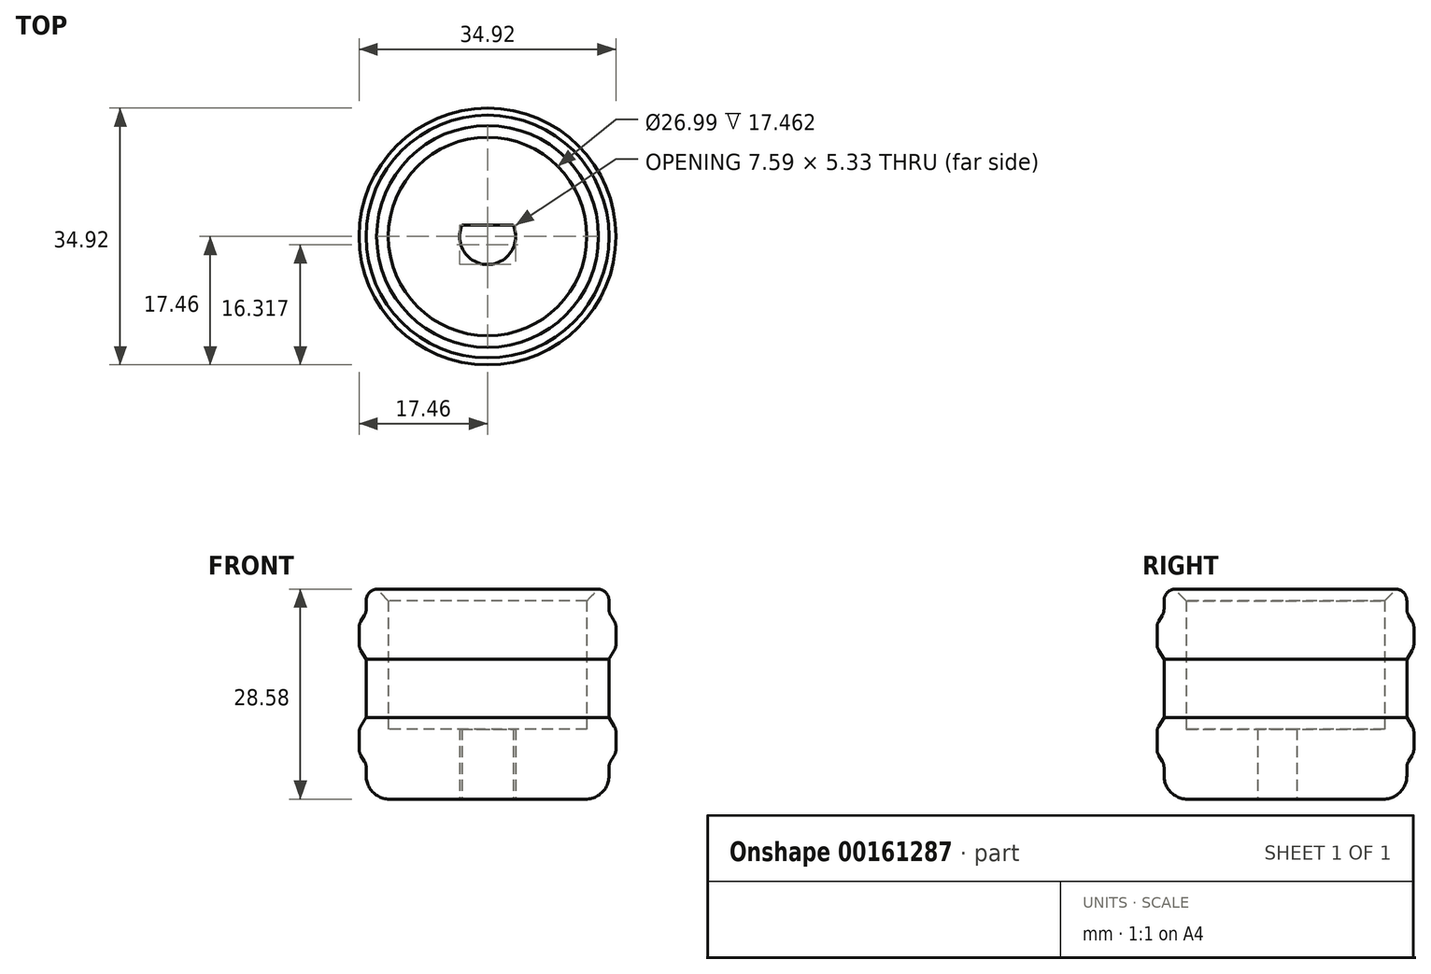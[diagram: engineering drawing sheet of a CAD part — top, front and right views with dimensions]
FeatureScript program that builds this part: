
annotation { "Feature Type Name" : "Feature", "Feature Type Description" : "" }
export const myFeature = defineFeature(function(context is Context, id is Id, definition is map)
    precondition{}
    {
        {
            var Q0;
            Q0=qCreatedBy(makeId("Top.planeOp"),FACE);
            var sketch = newSketch(context, id + "F0", { "sketchPlane" : qUnion([Q0])});
            skCircle(sketch, "E0", {"center": v(0, 0) * mm, "radius": 16.51 * mm});
            skArc(sketch, "E1", {"start": v(-3.5, 1.52) * mm, "mid": v(0, -3.81) * mm, "end": v(3.5, 1.52) * mm});
            skPoint(sketch, "E2", {"position": v(0, -3.81) * mm});
            skLineSegment(sketch, "E3", {"start": v(-3.5, 1.52) * mm, "end": v(3.5, 1.52) * mm});
            skSolve(sketch);
        }
        {
            var Q0;
            Q0=makeQuery(id+"F0.imprint","IMPRINT",FACE,{"disambiguationData":[TD([[makeQuery(id+"F0.imprint","IMPRINT",EDGE,{"derivedFrom":sQuery(id+"F0.wireOp",EDGE,"E0")}),1.0]])]});
            extrude(context, id + "F1", {"entities" : qUnion([Q0]), "depth" : 9.52 * mm, "offsetDistance" : 25.4 * mm});
        }
        {
            var Q0;
            Q0=makeQuery(id+"F1.opExtrude","CAP_FACE",FACE,{"disambiguationData":[OSD([sQuery(id+"F0.wireOp",EDGE,"E0"),sQuery(id+"F0.wireOp",EDGE,"E1"),sQuery(id+"F0.wireOp",EDGE,"E3")])],"isStart":false});
            var sketch = newSketch(context, id + "F2", { "sketchPlane" : qUnion([Q0])});
            skCircle(sketch, "E4", {"center": v(0, 0) * mm, "radius": 16.51 * mm});
            skCircle(sketch, "E5", {"center": v(0, 0) * mm, "radius": 13.5 * mm});
            skSolve(sketch);
        }
        {
            var Q0;
            Q0 = qSketchRegion(id + "F2", true);
            extrude(context, id + "F3", {"entities" : qUnion([Q0]), "operationType" : NewBodyOperationType.ADD, "depth" : 19.05 * mm, "offsetDistance" : 25.4 * mm});
        }
        {
            var Q0;
            Q0=makeQuery(id+"F3.opExtrude","CAP_EDGE",EDGE,{"disambiguationData":[OSD([sQuery(id+"F2.wireOp",EDGE,"E5")])],"isStart":false});
            chamfer(context, id + "F4", {"entities" : qUnion([Q0]), "width" : 1.59 * mm, "tangentPropagation" : true});
        }
        {
            var Q0;
            Q0=makeQuery(id+"F3.opExtrude","CAP_EDGE",EDGE,{"disambiguationData":[OSD([sQuery(id+"F2.wireOp",EDGE,"E4")])],"isStart":false});
            fillet(context, id + "F5", {"entities" : qUnion([Q0]), "radius" : 1.59 * mm, "tangentPropagation" : true, "allowEdgeOverflow" : false});
        }
        {
            var Q0;
            Q0=makeQuery(id+"F1.opExtrude","CAP_EDGE",EDGE,{"disambiguationData":[OSD([sQuery(id+"F0.wireOp",EDGE,"E0")])],"isStart":true});
            fillet(context, id + "F6", {"entities" : qUnion([Q0]), "radius" : 3.17 * mm, "tangentPropagation" : true, "allowEdgeOverflow" : false});
        }
        {
            var Q0;
            Q0=qCreatedBy(makeId("Right.planeOp"),FACE);
            var sketch = newSketch(context, id + "F7", { "sketchPlane" : qUnion([Q0])});
            skLineSegment(sketch, "E6", {"start": v(16.51, 25.4) * mm, "end": v(17.46, 23.81) * mm});
            skLineSegment(sketch, "E7", {"start": v(17.46, 23.81) * mm, "end": v(17.46, 20.64) * mm});
            skLineSegment(sketch, "E8", {"start": v(17.46, 20.64) * mm, "end": v(16.51, 19.05) * mm});
            skLineSegment(sketch, "E9", {"start": v(16.51, 19.05) * mm, "end": v(16.51, 25.4) * mm});
            skLineSegment(sketch, "E10", {"start": v(16.51, 11.11) * mm, "end": v(16.51, 4.76) * mm});
            skLineSegment(sketch, "E11", {"start": v(16.51, 4.76) * mm, "end": v(17.46, 6.35) * mm});
            skLineSegment(sketch, "E12", {"start": v(17.46, 6.35) * mm, "end": v(17.46, 9.53) * mm});
            skLineSegment(sketch, "E13", {"start": v(16.51, 11.11) * mm, "end": v(17.46, 9.53) * mm});
            skLineSegment(sketch, "E14", {"start": v(0, 41.62) * mm, "end": v(0, -11.38) * mm, "construction": true});
            skPoint(sketch, "E15", {"position": v(16.51, 22.22) * mm});
            skPoint(sketch, "E16", {"position": v(17.46, 22.22) * mm});
            skPoint(sketch, "E17", {"position": v(17.46, 7.94) * mm});
            skPoint(sketch, "E18", {"position": v(16.51, 7.94) * mm});
            skSolve(sketch);
        }
        {
            var Q0;
            Q0=makeQuery(id+"F7.imprint","IMPRINT",FACE,{"disambiguationData":[TD([[makeQuery(id+"F7.imprint","IMPRINT",EDGE,{"derivedFrom":sQuery(id+"F7.wireOp",EDGE,"E6")}),-1.0]])]});
            var Q1;
            Q1=makeQuery(id+"F7.imprint","IMPRINT",FACE,{"disambiguationData":[TD([[makeQuery(id+"F7.imprint","IMPRINT",EDGE,{"derivedFrom":sQuery(id+"F7.wireOp",EDGE,"E10")}),1.0]])]});
            var Q2;
            Q2=sQuery(id+"F7.wireOp",EDGE,"E14");
            revolve(context, id + "F8", {"operationType" : NewBodyOperationType.ADD, "surfaceOperationType" : NewSurfaceOperationType.NEW, "entities" : qUnion([Q0, Q1]), "axis" : qUnion([Q2]), "revolveType" : RevolveType.FULL});
        }
        {
            var Q0;
            Q0=makeQuery(id+"F8.opRevolve","SWEPT_EDGE",EDGE,{"disambiguationData":[OSD([sQuery(id+"F7.wireOp",EDGE,"E6"),sQuery(id+"F7.wireOp",EDGE,"E7")])]});
            var Q1;
            Q1=makeQuery(id+"F8.opRevolve","SWEPT_EDGE",EDGE,{"disambiguationData":[OSD([sQuery(id+"F7.wireOp",EDGE,"E6"),sQuery(id+"F7.wireOp",EDGE,"E9")])]});
            var Q2;
            Q2=makeQuery(id+"F8.opRevolve","SWEPT_EDGE",EDGE,{"disambiguationData":[OSD([sQuery(id+"F7.wireOp",EDGE,"E7"),sQuery(id+"F7.wireOp",EDGE,"E8")])]});
            var Q3;
            Q3=makeQuery(id+"F8.opRevolve","SWEPT_EDGE",EDGE,{"disambiguationData":[OSD([sQuery(id+"F7.wireOp",EDGE,"E8"),sQuery(id+"F7.wireOp",EDGE,"E9")])]});
            var Q4;
            Q4=makeQuery(id+"F8.opRevolve","SWEPT_EDGE",EDGE,{"disambiguationData":[OSD([sQuery(id+"F7.wireOp",EDGE,"E10"),sQuery(id+"F7.wireOp",EDGE,"E13")])]});
            var Q5;
            Q5=makeQuery(id+"F8.opRevolve","SWEPT_EDGE",EDGE,{"disambiguationData":[OSD([sQuery(id+"F7.wireOp",EDGE,"E12"),sQuery(id+"F7.wireOp",EDGE,"E13")])]});
            var Q6;
            Q6=makeQuery(id+"F8.opRevolve","SWEPT_EDGE",EDGE,{"disambiguationData":[OSD([sQuery(id+"F7.wireOp",EDGE,"E11"),sQuery(id+"F7.wireOp",EDGE,"E12")])]});
            var Q7;
            Q7=makeQuery(id+"F8.opRevolve","SWEPT_EDGE",EDGE,{"disambiguationData":[OSD([sQuery(id+"F7.wireOp",EDGE,"E10"),sQuery(id+"F7.wireOp",EDGE,"E11")])]});
            fillet(context, id + "F9", {"entities" : qUnion([Q0, Q1, Q2, Q3, Q4, Q5, Q6, Q7]), "radius" : 1.59 * mm, "tangentPropagation" : true, "allowEdgeOverflow" : false});
        }
    });
